# Revit family: POR_Ulysse_E0566_BIM_FR
name_source: partatom
category: Plumbing Fixtures
revit_build: Autodesk Revit 2017 (Build: 20160225_1515(x64)
units: mm (PartAtom-declared; Revit-internal decimal feet)

## family parameters
Always vertical = No
Cut with Voids When Loaded = No
OmniClass Number = 23.45.05.14.21.11
OmniClass Title = Bath/Shower Units
Part Type = Normal
Room Calculation Point = No
Round Connector Dimension = Use Diameter
Shared = No
Work Plane-Based = No

## types (1)
- E0566TI - ULYSSE - 30 x 23,5 x (H) 150 cm
    Accessoires = http://www.porcher.com
    Auteur = Ideal Standard
    BIMobject main category = Sanitary
    BIMobject main category code = sanitary
    BOSUseNativeGeometries = 1
    Bim-NomDuProjet = POR_Porcher_Basins_E0566TI
    Brand url = http://www.porcher.com
    Caractéristiques = 30 x 23,5 x (H) 150 cm -
    CodeBarre = 5017830506409
    Conformité = NF
    ConseilsDInstallation = www.idealspec.fr
    Cost = 0 $
    Couleur = TI
    CoûtDeRemplacement = 0
    Date of publishing = 2018_05_23
    DateDeCréation = 2018_05_23
    Description = ULYSSE - 30 x 23,5 x (H) 150 cm
    Dimensions = 300 x 248 x 1500 mm
    DuréeGarantie = ans
    DétailGarantie = Constructeur
    EAN code = https://5017830506409
    Edition number = 1
    Espace = Interne
    Forme = Complexe
    Hauteur = 1500 mm  [stored 4.92126 ft]
    IFC Classification = Sanitary Terminal
    IfcExportAs = IfcSanitaryTerminalType
    IfcExportType = Basins
    InformationsProduit = www.idealspec.fr
    Installation instructions = http://www.idealspec.fr
    Largeur = 300 mm
    Longueur = 248 mm
    Manufacturer name = Porcher
    Marque = PORCHER
    Material main = Ceramics
    Matériel = Ceramics
    Model = E0566TI
    NBS Reference Code = 31-79
    NBS Reference Description = Sinks, Wash Basins And Troughs
    Nom = POR_Porcher_Basins_E0566TI
    Nominal height = 330
    Nominal width = 265
    OmniClass Code = 23-31 13 00
    OmniClass Description = Sinks
    PerformanceAccessibilité = NF
    PoidsNet = 18.05 Kg
    Product Guid = 2fb3d5ee-5b94-4a7e-82b1-0b00ad6ceddc
    Product SKU = E0566
    Product certification = http://www.idealspec.fr
    Product data url = https://bimobject.com
    Product family = ULYSSE
    Product group = Basins
    Product name = ULYSSE - 30 x 23,5 x (H) 150 cm
    Product url = http://www.idealspec.fr
    Profondeur = 0 mm  [stored 0 ft]
    QR code = http://bimobject.com
    Raccordement = Plomberie
    Référence = E0566TI
    Révision = 1
    Technical description = http://www.idealspec.fr
    TypeDImmobilisation = Fixe
    URL = http://www.porcher.com
    Uniclass 1.4 Code = L7212
    Uniclass 1.4 Description = Washbasins
    Uniclass 2015 Code = Pr_40_20_96
    Uniclass 2015 Name = Wash basins, sinks and troughs
    Uniclass2015Code = Pr_40_20_96
    Uniclass2015Title = Wash basins, sinks and troughs
    Uniclass2015Version = Products v1.1
    UnitéDeTemps = an
    UrlDuFabricant = http://www.porcher.com
    Version = 1
    Weight Net (Kg) = 18.05

note: [stored X ft] marks values corroborated as IEEE doubles in the binary element streams (Revit-internal decimal feet)

## geometry (parser evidence)
native form markers: Sweep x2
no freeform markers — native parametric forms only
